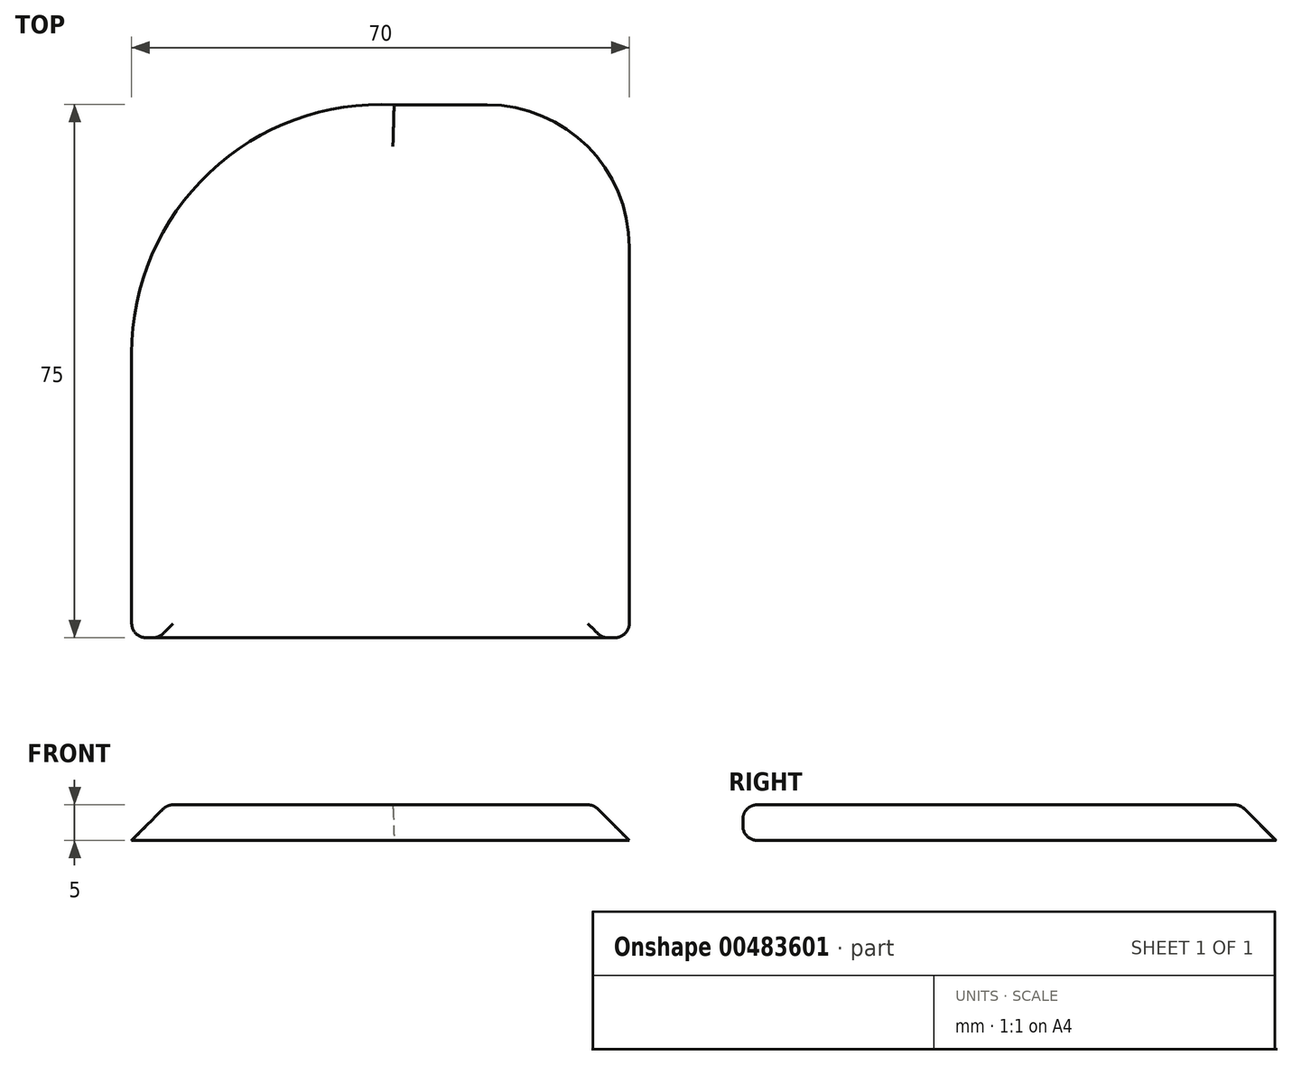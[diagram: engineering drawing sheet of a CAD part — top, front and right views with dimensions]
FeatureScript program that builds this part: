
annotation { "Feature Type Name" : "Feature", "Feature Type Description" : "" }
export const myFeature = defineFeature(function(context is Context, id is Id, definition is map)
    precondition{}
    {
        {
            var Q0;
            Q0=qCreatedBy(makeId("Top.planeOp"),FACE);
            var sketch = newSketch(context, id + "F0", { "sketchPlane" : qUnion([Q0])});
            skLineSegment(sketch, "E0", {"start": v(0, 40) * mm, "end": v(0, 0) * mm});
            skLineSegment(sketch, "E1", {"start": v(0, 0) * mm, "end": v(70, 0) * mm});
            skLineSegment(sketch, "E2", {"start": v(70, 0) * mm, "end": v(70, 54.95) * mm});
            skArc(sketch, "E3", {"start": v(0, 40) * mm, "mid": v(10.94, 65.42) * mm, "end": v(36.93, 74.95) * mm});
            skArc(sketch, "E4", {"start": v(70, 54.95) * mm, "mid": v(64.14, 69.09) * mm, "end": v(50, 74.95) * mm});
            skLineSegment(sketch, "E5", {"start": v(36.93, 74.95) * mm, "end": v(50, 74.95) * mm});
            skSolve(sketch);
        }
        {
            var Q0;
            Q0 = qSketchRegion(id + "F0", true);
            extrude(context, id + "F1", {"entities" : qUnion([Q0]), "depth" : 5 * mm});
        }
        {
            var Q0;
            Q0=makeQuery(id+"F1.opExtrude","CAP_EDGE",EDGE,{"disambiguationData":[OSD([sQuery(id+"F0.wireOp",EDGE,"E4")])],"isStart":false});
            var Q1;
            Q1=makeQuery(id+"F1.opExtrude","CAP_EDGE",EDGE,{"disambiguationData":[OSD([sQuery(id+"F0.wireOp",EDGE,"E3")])],"isStart":false});
            chamfer(context, id + "F2", {"entities" : qUnion([Q0, Q1]), "width" : 5 * mm, "tangentPropagation" : true});
        }
        {
            var Q0;
            Q0=makeQuery(id+"F1.opExtrude","CAP_EDGE",EDGE,{"disambiguationData":[OSD([sQuery(id+"F0.wireOp",EDGE,"E1")])],"isStart":true});
            var Q1;
            Q1=makeQuery(id+"F1.opExtrude","CAP_FACE",FACE,{"disambiguationData":[OSD([sQuery(id+"F0.wireOp",EDGE,"E0"),sQuery(id+"F0.wireOp",EDGE,"E1"),sQuery(id+"F0.wireOp",EDGE,"E2"),sQuery(id+"F0.wireOp",EDGE,"E3"),sQuery(id+"F0.wireOp",EDGE,"E4"),sQuery(id+"F0.wireOp",EDGE,"E5")])],"isStart":false});
            fillet(context, id + "F3", {"entities" : qUnion([Q0, Q1]), "radius" : 2 * mm, "tangentPropagation" : true, "allowEdgeOverflow" : false});
        }
    });
